# Revit family: Schityvatel-Ekh vzryvozashchishchennyy RD-26 AYaKS
name_source: partatom
category: Датчики
units: mm (PartAtom-declared; Revit-internal decimal feet)

## family parameters
Всегда вертикально = Да
Заголовок OmniClass = Communication and Data Processing Equipment
На основе рабочей плоскости = Нет
Номер OmniClass = 23.85.50.17
Общий = Нет
При загрузке вырезать с полостями = Нет
Размер круглого соединителя = Использовать диаметр
Сохранять ориентацию аннотаций = Нет
Тип детали = Нормальный
Точка принадлежности помещению = Нет

## types (1)
- Считыватель-Ех взрывозащищенный RD-26 АЯКС
    ADSK_Единица измерения = шт.
    ADSK_Завод-изготовитель = ООО НПП «МАГНИТО-КОНТАКТ»
    ADSK_Материал = Нержавеющая сталь
    ADSK_Наименование = Считыватель-Ех взрывозащищенный RD-26 АЯКС РВ EX MB I MB X / 1EX MB IIC T5 GB X / EX MB IIIC T80°C DB X ИЛИ 1EX MB IIC T5 GB X / EX MB IIIC T80°C DB X
    ADSK_Наименование краткое = Считыватель-Ех взрывозащищенный RD-26 АЯКС
    ADSK_Обозначение = АТФЕ.425728.210ПС
    ADSK_Примечание = Считыватель имеет маркировку взрывозащиты по взрывоопасным газовым и пылевым средам РВ Ex mb I Mb X / 1Ex mb IIC T5 Gb X / Ex mb IIIC T80°C Db X или 1Ex mb IIC T5 Gb X / Ex mb IIIC T80°C Db X
    ADSK_Размер_Высота = 30 мм
    ADSK_Размер_Диаметр = 6 мм
    ADSK_Размер_Длина = 115 мм
    ADSK_Размер_Длина вывода = 1000 мм
    ADSK_Размер_Ширина = 60 мм
    URL = https://m-kontakt.ru
    Атмосферное давление, кПа = от 84 до 106.7
    Вставка = Пластик
    Дальность чтения, см = 6-14 (для REH), 3-6 (для RMF)
    Изготовитель = ООО НПП «МАГНИТО-КОНТАКТ»
    Климатическое исполнение по ГОСТ 15150 = УХЛ3.1
    Напряжение питания, В = 8 - 18
    Описание = Считыватель-Ех взрывозащищенный RD-26 АЯКС (далее - считыватель) предназначен для применения в системах безопасности объектов и сетевых системах контроля и управления доступом (СКУД), в качестве устройства считывания бесконтактных идентификаторов.
    Отметка по умолчанию = 0 мм
    Потребляемы ток, мА = 50
    Рабочая температура, °C = от -40 до +60
    Рабочая частота = 125 кГц (для REH), 13,56 МГц (для RMF)
    Средний срок службы, лет, не менее = 8
    Степень защиты оболочки по ГОСТ 14254 = IP66/IP67
    Чтение идентификаторов = HID ProxCard II, EM-Marine (для REH),Mifare Ultralight, Mifare Standard (Classic) 1K и 4К, Mifare ID (для RMF)
